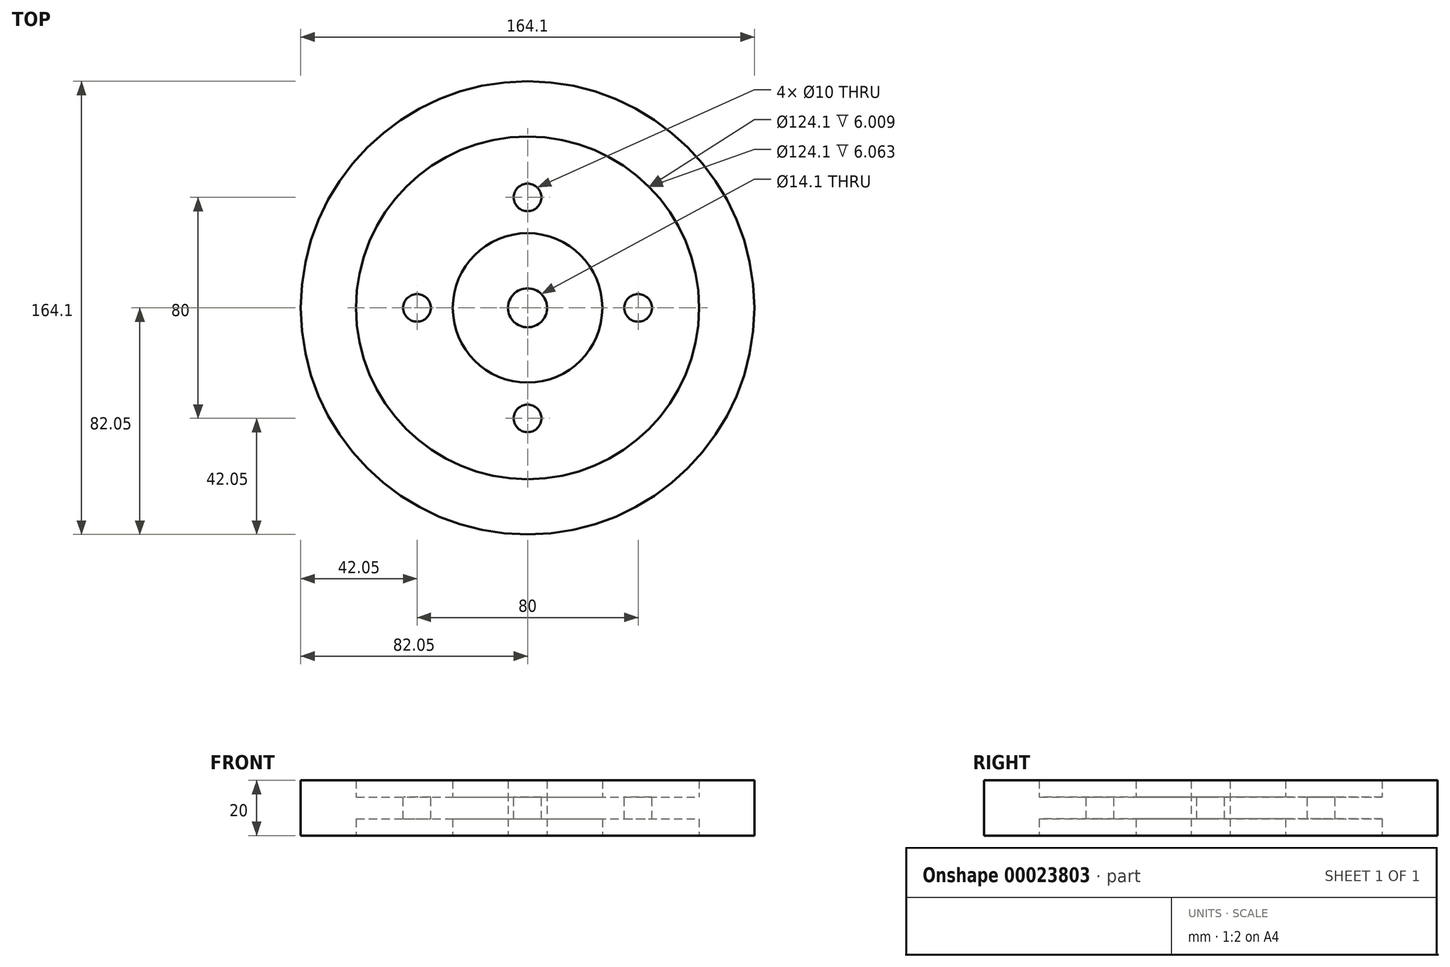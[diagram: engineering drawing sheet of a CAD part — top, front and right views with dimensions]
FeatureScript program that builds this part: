
annotation { "Feature Type Name" : "Feature", "Feature Type Description" : "" }
export const myFeature = defineFeature(function(context is Context, id is Id, definition is map)
    precondition{}
    {
        {
            var Q0;
            Q0=qCreatedBy(makeId("Front.planeOp"),FACE);
            var sketch = newSketch(context, id + "F0", { "sketchPlane" : qUnion([Q0])});
            skLineSegment(sketch, "E0", {"start": v(0, -30.02) * mm, "end": v(0, 36.71) * mm, "construction": true});
            skLineSegment(sketch, "E1.bottom", {"start": v(7.05, 8.83) * mm, "end": v(27.05, 8.83) * mm});
            skLineSegment(sketch, "E1.top", {"start": v(7.05, -11.17) * mm, "end": v(27.05, -11.17) * mm});
            skLineSegment(sketch, "E1.left", {"start": v(7.05, 8.83) * mm, "end": v(7.05, -11.17) * mm});
            skLineSegment(sketch, "E1.right", {"start": v(27.05, 8.83) * mm, "end": v(27.05, -11.17) * mm});
            skLineSegment(sketch, "E2.bottom", {"start": v(62.05, 8.83) * mm, "end": v(82.05, 8.83) * mm});
            skLineSegment(sketch, "E2.top", {"start": v(62.05, -11.17) * mm, "end": v(82.05, -11.17) * mm});
            skLineSegment(sketch, "E2.left", {"start": v(62.05, 8.83) * mm, "end": v(62.05, -11.17) * mm});
            skLineSegment(sketch, "E2.right", {"start": v(82.05, 8.83) * mm, "end": v(82.05, -11.17) * mm});
            skLineSegment(sketch, "E3.bottom", {"start": v(27.05, 2.76) * mm, "end": v(62.05, 2.76) * mm});
            skLineSegment(sketch, "E3.top", {"start": v(27.05, -5.16) * mm, "end": v(62.05, -5.16) * mm});
            skLineSegment(sketch, "E3.left", {"start": v(27.05, 2.76) * mm, "end": v(27.05, -5.16) * mm});
            skLineSegment(sketch, "E3.right", {"start": v(62.05, 2.76) * mm, "end": v(62.05, -5.16) * mm});
            skSolve(sketch);
        }
        {
            var Q0;
            {var subQ3=sQuery(id+"F0.wireOp",EDGE,"E1.bottom");Q0=makeQuery(id+"F0.imprint","IMPRINT",FACE,{"disambiguationData":[TD([[makeQuery(id+"F0.imprint","IMPRINT",EDGE,{"derivedFrom":subQ3}),-1.0]])]});}
            var Q1;
            Q1=makeQuery(id+"F0.imprint","IMPRINT",FACE,{"disambiguationData":[TD([[makeQuery(id+"F0.imprint","IMPRINT",EDGE,{"derivedFrom":sQuery(id+"F0.wireOp",EDGE,"E3.bottom")}),-1.0]])]});
            var Q2;
            {var subQ3=sQuery(id+"F0.wireOp",EDGE,"E2.bottom");Q2=makeQuery(id+"F0.imprint","IMPRINT",FACE,{"disambiguationData":[TD([[makeQuery(id+"F0.imprint","IMPRINT",EDGE,{"derivedFrom":subQ3}),-1.0]])]});}
            var Q3;
            Q3=sQuery(id+"F0.wireOp",EDGE,"E0");
            revolve(context, id + "F1", {"entities" : qUnion([Q0, Q1, Q2]), "axis" : qUnion([Q3]), "revolveType" : RevolveType.FULL});
        }
        {
            var Q0;
            Q0=makeQuery(id+"F1.opRevolve","SWEPT_FACE",FACE,{"disambiguationData":[OSD([sQuery(id+"F0.wireOp",EDGE,"E3.bottom")])]});
            var sketch = newSketch(context, id + "F2", { "sketchPlane" : qUnion([Q0])});
            skCircle(sketch, "E4", {"center": v(0, 40) * mm, "radius": 5 * mm});
            skCircle(sketch, "E5.1.0", {"center": v(-40, 0) * mm, "radius": 5 * mm});
            skCircle(sketch, "E5.2.0", {"center": v(0, -40) * mm, "radius": 5 * mm});
            skCircle(sketch, "E5.3.0", {"center": v(40, 0) * mm, "radius": 5 * mm});
            skPoint(sketch, "E5.center", {"position": v(0, 0) * mm});
            skSolve(sketch);
        }
        {
            var Q0;
            Q0=makeQuery(id+"F2.imprint","IMPRINT",FACE,{"disambiguationData":[TD([[makeQuery(id+"F2.imprint","IMPRINT",EDGE,{"derivedFrom":sQuery(id+"F2.wireOp",EDGE,"E4")}),1.0]])]});
            var Q1;
            Q1=makeQuery(id+"F2.imprint","IMPRINT",FACE,{"disambiguationData":[TD([[makeQuery(id+"F2.imprint","IMPRINT",EDGE,{"derivedFrom":sQuery(id+"F2.wireOp",EDGE,"E5.3.0")}),1.0]])]});
            var Q2;
            Q2=makeQuery(id+"F2.imprint","IMPRINT",FACE,{"disambiguationData":[TD([[makeQuery(id+"F2.imprint","IMPRINT",EDGE,{"derivedFrom":sQuery(id+"F2.wireOp",EDGE,"E5.2.0")}),1.0]])]});
            var Q3;
            Q3=makeQuery(id+"F2.imprint","IMPRINT",FACE,{"disambiguationData":[TD([[makeQuery(id+"F2.imprint","IMPRINT",EDGE,{"derivedFrom":sQuery(id+"F2.wireOp",EDGE,"E5.1.0")}),1.0]])]});
            extrude(context, id + "F3", {"entities" : qUnion([Q0, Q1, Q2, Q3]), "operationType" : NewBodyOperationType.REMOVE, "oppositeDirection" : true, "depth" : 25 * mm});
        }
    });
